# Revit family: Xbeam - 10m Beam + Brackets
name_source: partatom
category: Structural Framing
revit_build: Autodesk Revit 2017 (Build: 20181011_1645(x64)
units: mm (PartAtom-declared; Revit-internal decimal feet)

## family parameters
Always export as geometry = No
Always vertical = Yes
Cut with Voids When Loaded = No
Material for Model Behavior = Other
Section Shape = Not Defined
Shared = No
Show family pre-cut in plan views = Yes
Structural Framing Length Roundoff = 0 mm
Work Plane-Based = No

## types (1)
- Xbeam - 10m Beam + Brackets
    Distancia a borde = 20000 mm  [stored 65.6168 ft]
    Distancia maxima = 568 mm
    Min. Max. Portal spacing = 9000 mm
    Min. Max. Primary Bearer Lenght = 10000 mm  [stored 32.8084 ft]
    Min. Max. distancia a borde = 568 mm
    Portal spacing = 15000 mm  [stored 49.2126 ft]
    Primary Bearer Lenght = 10000 mm  [stored 32.8084 ft]
    numero de pilares = 2

note: [stored X ft] marks values corroborated as IEEE doubles in the binary element streams (Revit-internal decimal feet)

## geometry (parser evidence)
native form markers: Sweep x26
no freeform markers — native parametric forms only
